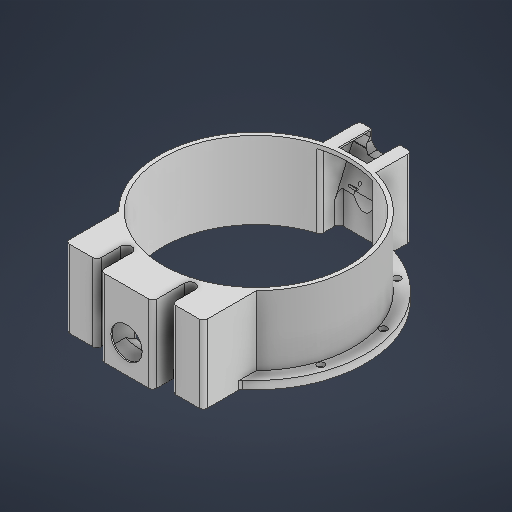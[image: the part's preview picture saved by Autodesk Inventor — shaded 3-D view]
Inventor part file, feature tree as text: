
AUTODESK INVENTOR PART (.ipt)
format: ipt  version: 2025 (Build 290162000, 162)  size: 761,856 bytes
history: native  units: in
note: dims shown in document units (in); Inventor stores cm internally (conversion verified against a paired STEP export)
features: extrude x28, sketch x20, chamfer x4, other x3, plane x3, fillet x2
ambient origin geometry x8: Origin, YZ Plane, XZ Plane, XY Plane, X Axis, Y Axis, Z Axis, Center Point
bodies: Body1 (feature_tree)
feature tree (60):
  other  "Cylinder.ipt"
  extrude  "Extrusion1"  Depth=0.3937in
  extrude  "Extrusion2"  Depth=0.3937in TaperAngle=0.0deg
  sketch  "Sketch3"  dims[d7=11.2205in d8=10.6299in]
  extrude  "Extrusion3"  Depth=10.6299in
  extrude  "Extrusion5"  Depth=0.1969in TaperAngle=0.0deg
  sketch  "Sketch6"  dims[d24=0.1969in d25=0.0in d31=0.0in d32=0.0in]
  extrude  "Extrusion6"  Depth=0.2953in
  extrude  "Extrusion7"  TaperAngle=0.0deg  [1 undecoded]
  extrude  "Extrusion8"  Depth=9.8425in
  plane  "Work Plane1"
  extrude  "Extrusion9"  Depth=9.065in
  extrude  "Extrusion21"  Depth=0.3937in
  sketch  "Sketch18"  dims[d107=2.2047in d108=0.0in d111=3.937in d112=0.0in]
  extrude  "Extrusion22"  Depth=3.937in TaperAngle=0.0deg
  sketch  "Sketch19"  dims[d113=2.5591in d115=2.2047in d116=0.0in]
  extrude  "Extrusion23"  Depth=2.2047in TaperAngle=0.0deg
  extrude  "Extrusion27"  Depth=0.5433in
  extrude  "Extrusion31"  Depth=0.0787in
  extrude  "Extrusion32"  TaperAngle=0.0deg  [1 undecoded]
  extrude  "Extrusion33"  Depth=0.0787in
  extrude  "Extrusion34"  TaperAngle=90.0deg  [1 undecoded]
  extrude  "Extrusion40"  Depth=4.1339in TaperAngle=0.0deg
  extrude  "Extrusion42"  Depth=0.0787in
  extrude  "Extrusion43"  Depth=1.378in
  extrude  "Extrusion44"  Depth=0.1969in
  extrude  "Extrusion45"  Depth=0.1969in TaperAngle=360.0deg
  chamfer  "Chamfer8"  Distance=10.4151in
  sketch  "Sketch31"  dims[d164=1.5298in d165=0.0787in]
  extrude  "Extrusion46"  Depth=0.1969in
  extrude  "Extrusion47"  Depth=0.3937in TaperAngle=0.0deg
  plane  "Work Plane2"
  extrude  "Extrusion48"  Depth=0.1969in
  plane  "Work Plane3"
  sketch  "Sketch33"  dims[d169=2.2047in d170=0.0in d171=4.1339in d172=0.0in]
  extrude  "Extrusion49"  Depth=0.1969in
  extrude  "Extrusion50"  Depth=0.1969in
  extrude  "Extrusion51"  Depth=0.1969in
  extrude  "Extrusion52"  Depth=0.1969in
  chamfer  "Chamfer9"  Distance=3.5433in
  chamfer  "Chamfer10"  Distance=3.1693in
  fillet  "Fillet19"  Radius=3.1693in
  fillet  "Fillet20"  Radius=0.3937in
  chamfer  "Chamfer11"  Distance=0.9843in
  other  "Solid12::Cylinder.ipt"
  other  "TaggingFeature1"
  sketch  "Sketch1"  dims[d0=0.3937in d2=10.2362in]
  sketch  "Sketch2"  dims[d3=0.0in d4=0.0in d5=0.3937in d6=0.0in]
  sketch  "Sketch5"  dims[d17=10.6299in d18=0.2953in]
  sketch  "Sketch7"  dims[d33=2.1654in d34=0.0in d35=9.8425in]
  sketch  "Sketch9"  dims[d36=10.6299in d46=9.065in]
  sketch  "Sketch14"  dims[d47=0.3937in d48=0.0in d88=0.0787in]
  sketch  "Sketch22"  dims[d117=0.0591in d120=0.5433in]
  sketch  "Sketch Circular Pattern3"  dims[d10=0.1969in d11=0.0in d15=0.1969in d16=0.0in]
  sketch  "Sketch28"  dims[d122=9.4488in d134=0.0787in]
  sketch  "Sketch30"  dims[d141=0.3937in d142=0.0in d159=0.0in d160=0.0in]
  sketch  "Sketch32"  dims[d166=1.8325in d167=90.0deg]
  sketch  "Sketch34"  dims[d173=1.1614in d174=0.0in d175=0.0787in]
  sketch  "Sketch35"  dims[d207=1.5157in d208=1.378in]
  sketch  "Sketch36"  dims[d209=0.2165in d210=0.3425in d211=3.937in d213=360.0deg d217=10.4151in d218=9.065in d221=0.3937in d222=0.0in d223=0.5433in d224=1.8228in d225=3.5433in d226=2.564in d227=2.7608in d228=3.5433in d231=3.1693in d232=0.0in d233=3.1693in d234=1.5846in d235=0.0in d236=0.0in d237=3.3661in d238=0.3937in d239=0.0in d240=0.0in d241=0.9843in d242=3.1496in d243=0.0in d244=1.5748in d245=0.0787in d246=0.1598in d247=0.4331in d248=0.1575in d249=0.1575in d250=0.1575in d251=0.9331in d252=0.3937in d254=0.3937in d255=0.9331in d256=0.4331in d257=0.4331in d258=2.1654in d259=0.0in d260=0.1772in d261=0.0in d262=0.315in d263=0.1666in d265=1.5871in d266=0.0in d267=1.4567in d268=0.5315in d269=-3.5433in d270=1.378in d271=1.378in d272=9.7638in d273=0.0787in d274=0.0in d275=0.6412in d276=0.0in d277=1.378in d278=0.0787in d279=1.5787in d280=0.0in d281=0.0787in d282=0.8268in d283=0.3937in d284=0.0787in d285=0.3937in d286=0.0463in d287=0.3937in d288=0.0787in d289=0.3937in d290=0.0463in d291=0.0787in d292=0.0in d293=1.378in d294=0.2756in d295=0.3076in d296=45.0deg d297=0.2756in d298=0.3076in d299=45.0deg d300=0.1969in d301=0.1969in d302=0.3381in d303=0.5576in d304=45.0deg d143=0.0197in d144=0.0344in d145=0.0197in d146=0.0344in d153=0.0in d154=0.0in d155=0.0in d156=0.0in d201=0.0197in d202=0.0344in d203=0.0197in d204=0.0344in d215=0.0197in d216=0.0344in]
note: 3 required parameter values undecoded (feature->parameter linkage not recoverable at this tier; creation-order binding heuristic only, values carry confidence <= 0.55)
